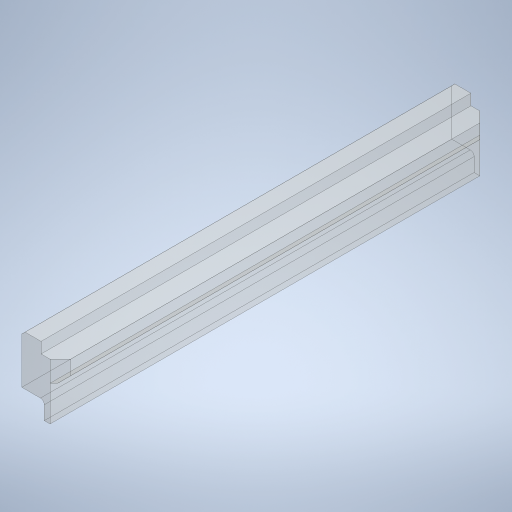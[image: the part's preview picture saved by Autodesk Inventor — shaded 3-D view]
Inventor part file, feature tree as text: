
AUTODESK INVENTOR PART (.ipt)
format: ipt  version: 2023 (Build 270158000, 158)  size: 287,744 bytes
history: native  units: mm
features: extrude x1, chamfer x1, sketch x1
ambient origin geometry x8: Origin, YZ Plane, XZ Plane, XY Plane, X Axis, Y Axis, Z Axis, Center Point
bodies: Solid1 (feature_tree)
feature tree (3):
  extrude  "Extrusion1"  Depth=2.5mm
  chamfer  "Chamfer1"  Distance=3.5mm
  sketch  "Sketch1"  dims[d0=12.0mm d1=2.5mm d2=3.5mm d3=6.0mm d4=1.7mm d5=3.0mm d6=67.0mm d7=0.0mm d8=6.0mm d9=5.5mm d14=1.6mm d15=0.6mm d16=1.0mm d17=1.0mm d18=0.5mm d19=0.5mm d20=1.6mm d21=2.0mm d22=45.0deg]
